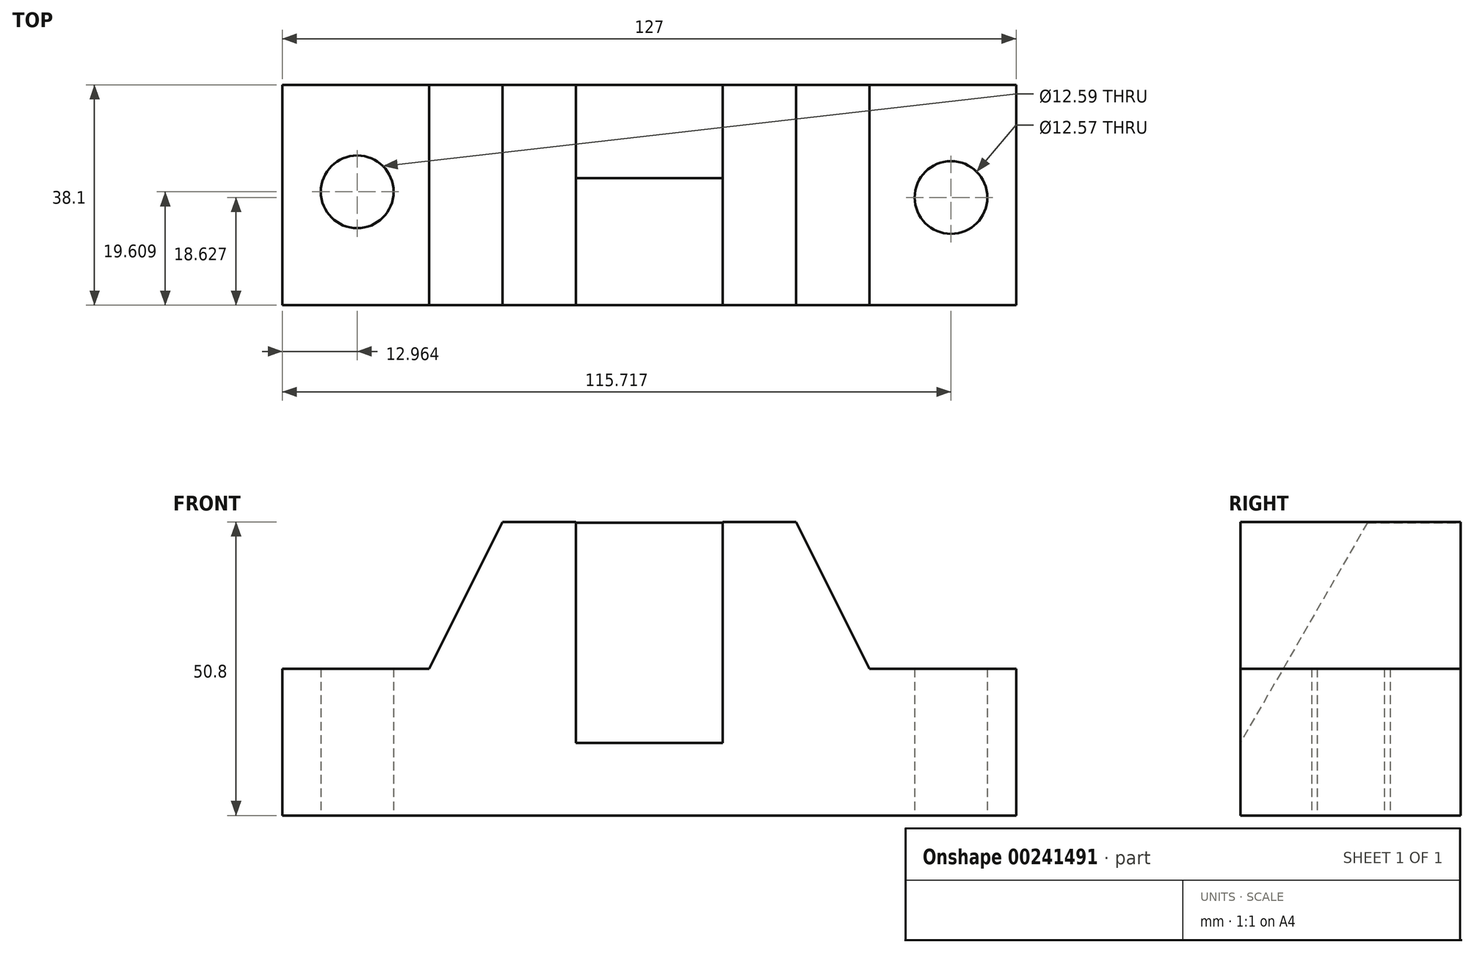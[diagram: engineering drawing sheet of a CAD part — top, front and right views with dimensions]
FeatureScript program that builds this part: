
annotation { "Feature Type Name" : "Feature", "Feature Type Description" : "" }
export const myFeature = defineFeature(function(context is Context, id is Id, definition is map)
    precondition{}
    {
        {
            var Q0;
            Q0=qCreatedBy(makeId("Front.planeOp"),FACE);
            var sketch = newSketch(context, id + "F0", { "sketchPlane" : qUnion([Q0])});
            skLineSegment(sketch, "E0", {"start": v(-62.05, 0) * mm, "end": v(64.95, 0) * mm});
            skLineSegment(sketch, "E1", {"start": v(64.95, 0) * mm, "end": v(64.95, 25.4) * mm});
            skLineSegment(sketch, "E2", {"start": v(64.95, 25.4) * mm, "end": v(39.55, 25.4) * mm});
            skLineSegment(sketch, "E3", {"start": v(39.55, 25.4) * mm, "end": v(26.85, 50.8) * mm});
            skLineSegment(sketch, "E4", {"start": v(26.85, 50.8) * mm, "end": v(14.15, 50.8) * mm});
            skLineSegment(sketch, "E5", {"start": v(14.15, 50.8) * mm, "end": v(14.15, 50.66) * mm});
            skLineSegment(sketch, "E6", {"start": v(14.15, 50.66) * mm, "end": v(-11.25, 50.66) * mm});
            skLineSegment(sketch, "E7", {"start": v(-11.25, 50.66) * mm, "end": v(-11.25, 50.8) * mm});
            skLineSegment(sketch, "E8", {"start": v(-11.25, 50.8) * mm, "end": v(-23.95, 50.8) * mm});
            skLineSegment(sketch, "E9", {"start": v(-23.95, 50.8) * mm, "end": v(-36.65, 25.4) * mm});
            skLineSegment(sketch, "E10", {"start": v(-36.65, 25.4) * mm, "end": v(-62.05, 25.4) * mm});
            skLineSegment(sketch, "E11", {"start": v(-62.05, 25.4) * mm, "end": v(-62.05, 0) * mm});
            skSolve(sketch);
        }
        {
            var Q0;
            Q0 = qSketchRegion(id + "F0", true);
            extrude(context, id + "F1", {"entities" : qUnion([Q0]), "depth" : 38.1 * mm});
        }
        {
            var Q0;
            Q0=qCreatedBy(makeId("Top.planeOp"),FACE);
            var sketch = newSketch(context, id + "F2", { "sketchPlane" : qUnion([Q0])});
            skCircle(sketch, "E12", {"center": v(-49.09, -18.5) * mm, "radius": 6.3 * mm});
            skCircle(sketch, "E13", {"center": v(53.67, -19.47) * mm, "radius": 6.29 * mm});
            skSolve(sketch);
        }
        {
            var Q0;
            Q0 = qSketchRegion(id + "F2", true);
            extrude(context, id + "F3", {"entities" : qUnion([Q0]), "operationType" : NewBodyOperationType.REMOVE, "depth" : 82.3 * mm});
        }
        {
            var Q0;
            Q0=makeQuery(id+"F1.opExtrude","CAP_EDGE",EDGE,{"disambiguationData":[OSD([sQuery(id+"F0.wireOp",EDGE,"E6")])],"isStart":false});
            chamfer(context, id + "F4", {"entities" : qUnion([Q0]), "chamferType" : ChamferType.OFFSET_ANGLE, "width" : 38.1 * mm, "oppositeDirection" : false, "angle" : 30 * degree, "tangentPropagation" : true});
        }
    });
